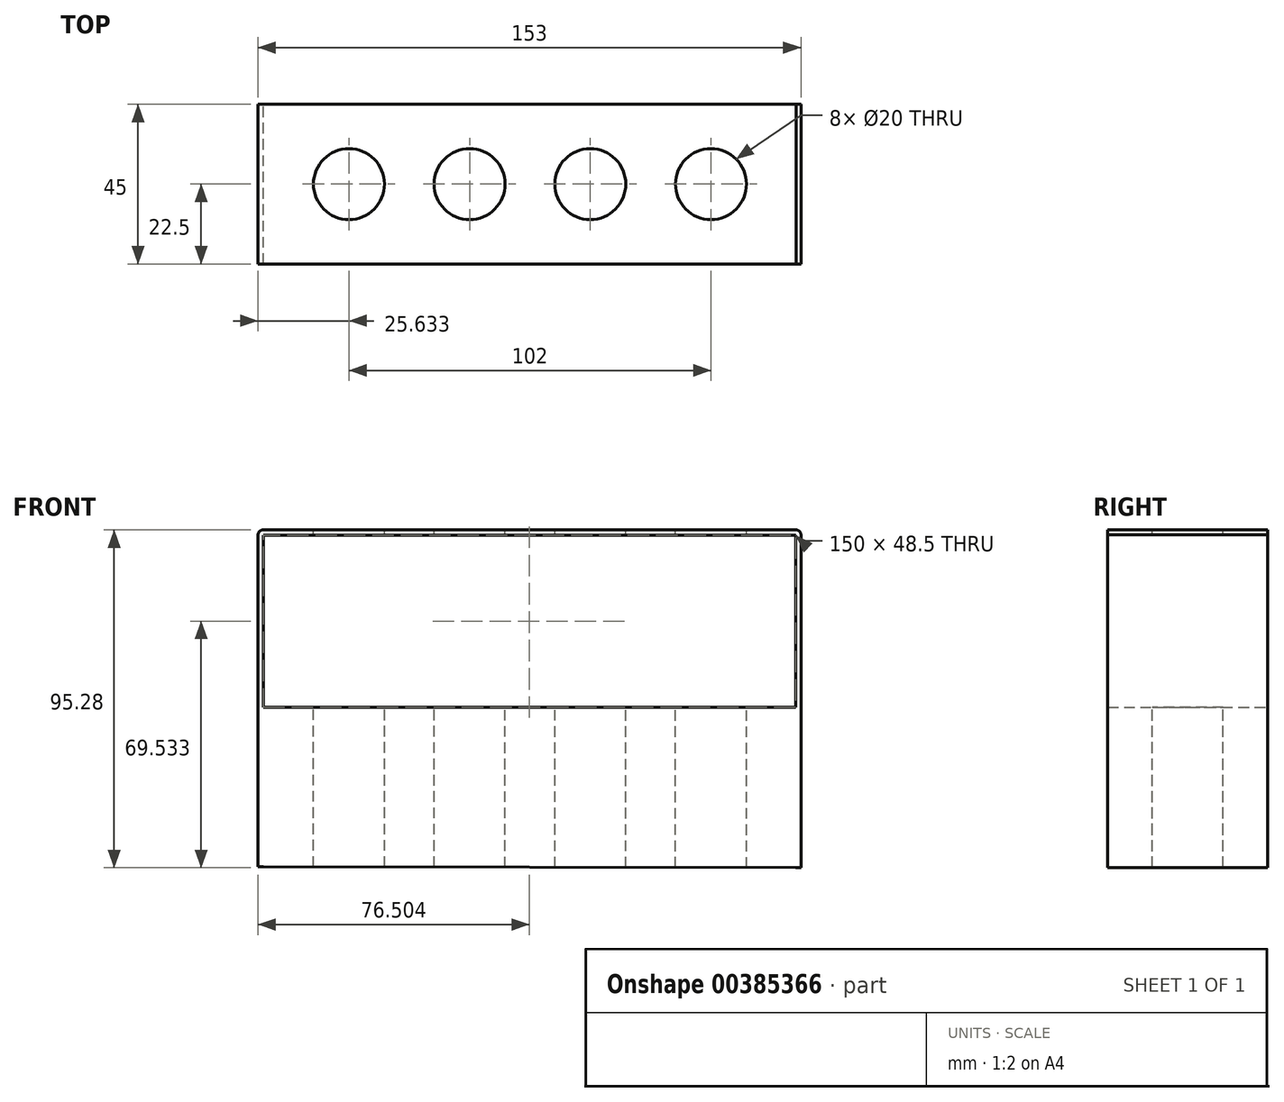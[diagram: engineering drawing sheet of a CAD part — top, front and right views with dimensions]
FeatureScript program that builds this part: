
annotation { "Feature Type Name" : "Feature", "Feature Type Description" : "" }
export const myFeature = defineFeature(function(context is Context, id is Id, definition is map)
    precondition{}
    {
        {
            var Q0;
            Q0=qCreatedBy(makeId("Front.planeOp"),FACE);
            var sketch = newSketch(context, id + "F0", { "sketchPlane" : qUnion([Q0])});
            skLineSegment(sketch, "E0", {"start": v(-75.29, -74.9) * mm, "end": v(-75.29, -29.9) * mm});
            skLineSegment(sketch, "E1", {"start": v(74.71, -29.9) * mm, "end": v(74.71, -75.19) * mm});
            skLineSegment(sketch, "E2", {"start": v(74.71, -75.19) * mm, "end": v(-75.29, -74.9) * mm});
            skLineSegment(sketch, "E3", {"start": v(-75.29, -29.9) * mm, "end": v(-75.29, 18.6) * mm});
            skLineSegment(sketch, "E4", {"start": v(-75.29, 20.1) * mm, "end": v(74.71, 20.1) * mm});
            skLineSegment(sketch, "E5", {"start": v(74.71, 18.6) * mm, "end": v(74.71, -29.9) * mm});
            skLineSegment(sketch, "E6", {"start": v(-75.29, -29.9) * mm, "end": v(74.71, -29.9) * mm});
            skLineSegment(sketch, "E7.0", {"start": v(-75.29, 18.6) * mm, "end": v(74.71, 18.6) * mm});
            skLineSegment(sketch, "E8.0", {"start": v(-76.79, -29.9) * mm, "end": v(-76.79, 18.6) * mm});
            skLineSegment(sketch, "E9.0", {"start": v(-76.79, -74.9) * mm, "end": v(-76.79, -29.9) * mm});
            skLineSegment(sketch, "E10", {"start": v(-76.79, -74.9) * mm, "end": v(-75.29, -74.9) * mm});
            skLineSegment(sketch, "E11.0", {"start": v(76.21, 18.72) * mm, "end": v(76.21, -29.9) * mm});
            skLineSegment(sketch, "E12.0", {"start": v(76.21, -29.9) * mm, "end": v(76.21, -75.19) * mm});
            skLineSegment(sketch, "E13", {"start": v(74.71, -75.19) * mm, "end": v(76.21, -75.19) * mm});
            skLineSegment(sketch, "E14", {"start": v(74.71, 20.1) * mm, "end": v(74.84, 20.1) * mm});
            skArc(sketch, "E15", {"start": v(-75.29, 20.1) * mm, "mid": v(-76.35, 19.65) * mm, "end": v(-76.79, 18.6) * mm});
            skArc(sketch, "E16", {"start": v(76.21, 18.46) * mm, "mid": v(75.78, 19.66) * mm, "end": v(74.59, 20.1) * mm});
            skSolve(sketch);
        }
        {
            var Q0;
            Q0=makeQuery(id+"F0.imprint","IMPRINT",FACE,{"disambiguationData":[TD([[makeQuery(id+"F0.imprint","IMPRINT",EDGE,{"derivedFrom":sQuery(id+"F0.wireOp",EDGE,"E0")}),-1.0]])]});
            extrude(context, id + "F1", {"entities" : qUnion([Q0]), "depth" : 22.5 * mm});
        }
        {
            var Q0;
            Q0=makeQuery(id+"F1.opExtrude","CAP_FACE",FACE,{"disambiguationData":[OSD([sQuery(id+"F0.wireOp",EDGE,"E0"),sQuery(id+"F0.wireOp",EDGE,"BdDkM7fl-LDPi-nAN3-AqWH-QST8wDYalAOm"),sQuery(id+"F0.wireOp",EDGE,"E1"),sQuery(id+"F0.wireOp",EDGE,"E2")])],"isStart":true});
            extrude(context, id + "F2", {"entities" : qUnion([Q0]), "operationType" : NewBodyOperationType.ADD, "depth" : 22.5 * mm});
        }
        {
            var Q0;
            Q0=makeQuery(id+"F0.imprint","IMPRINT",FACE,{"disambiguationData":[TD([[makeQuery(id+"F0.imprint","IMPRINT",EDGE,{"derivedFrom":sQuery(id+"F0.wireOp",EDGE,"E0")}),1.0]])]});
            extrude(context, id + "F3", {"entities" : qUnion([Q0]), "operationType" : NewBodyOperationType.ADD, "depth" : 22.5 * mm});
        }
        {
            var Q0;
            Q0=makeQuery(id+"F0.imprint","IMPRINT",FACE,{"disambiguationData":[TD([[makeQuery(id+"F0.imprint","IMPRINT",EDGE,{"derivedFrom":sQuery(id+"F0.wireOp",EDGE,"E0")}),1.0]])]});
            extrude(context, id + "F4", {"entities" : qUnion([Q0]), "operationType" : NewBodyOperationType.ADD, "oppositeDirection" : true, "depth" : 22.5 * mm});
        }
        {
            var Q0;
            {var subQ0=sQuery(id+"F0.wireOp",EDGE,"E14");var subQ1=sQuery(id+"F0.wireOp",EDGE,"E4");Q0=makeQuery(id+"F4.boolean.opBoolean","MERGE",FACE,{"derivedFrom":[makeQuery(id+"F3.opExtrude","SWEPT_FACE",FACE,{"disambiguationData":[OSD([subQ1,subQ0])]}),makeQuery(id+"F4.opExtrude","SWEPT_FACE",FACE,{"disambiguationData":[OSD([subQ1,subQ0])]})]});}
            var sketch = newSketch(context, id + "F5", { "sketchPlane" : qUnion([Q0])});
            skCircle(sketch, "E17", {"center": v(-51.16, 0) * mm, "radius": 10 * mm});
            skCircle(sketch, "E18", {"center": v(-17.16, 0) * mm, "radius": 10 * mm});
            skCircle(sketch, "E19", {"center": v(16.84, 0) * mm, "radius": 10 * mm});
            skCircle(sketch, "E20", {"center": v(50.84, 0) * mm, "radius": 10 * mm});
            skLineSegment(sketch, "E21", {"start": v(-41.16, 0) * mm, "end": v(-27.16, 0) * mm, "construction": true});
            skLineSegment(sketch, "E22", {"start": v(-7.16, 0) * mm, "end": v(6.84, 0) * mm, "construction": true});
            skLineSegment(sketch, "E23", {"start": v(26.84, 0) * mm, "end": v(40.84, 0) * mm, "construction": true});
            skSolve(sketch);
        }
        {
            var Q0;
            Q0=sQuery(id+"F5.wireOp",VERTEX,"E17.center");
            var Q1;
            Q1=sQuery(id+"F5.wireOp",VERTEX,"E18.center");
            var Q2;
            Q2=sQuery(id+"F5.wireOp",VERTEX,"E19.center");
            var Q3;
            Q3=sQuery(id+"F5.wireOp",VERTEX,"E20.center");
            var Q4;
            Q4=makeQuery(id+"F1.opExtrude","SWEPT_BODY",BODY,{"disambiguationData":[OSD([sQuery(id+"F0.wireOp",EDGE,"E0"),sQuery(id+"F0.wireOp",EDGE,"E1"),sQuery(id+"F0.wireOp",EDGE,"E2"),sQuery(id+"F0.wireOp",EDGE,"E6")])]});
            hole(context, id + "F6", {"style" : HoleStyle.SIMPLE, "endStyle" : HoleEndStyle.THROUGH, "holeDiameter" : 20 * mm, "isTappedThrough" : true, "tappedDepth" : 12 * mm, "tapClearance" : 3, "locations" : qUnion([Q0, Q1, Q2, Q3]), "scope" : qUnion([Q4]), "majorDiameter" : 5 * mm});
        }
    });
